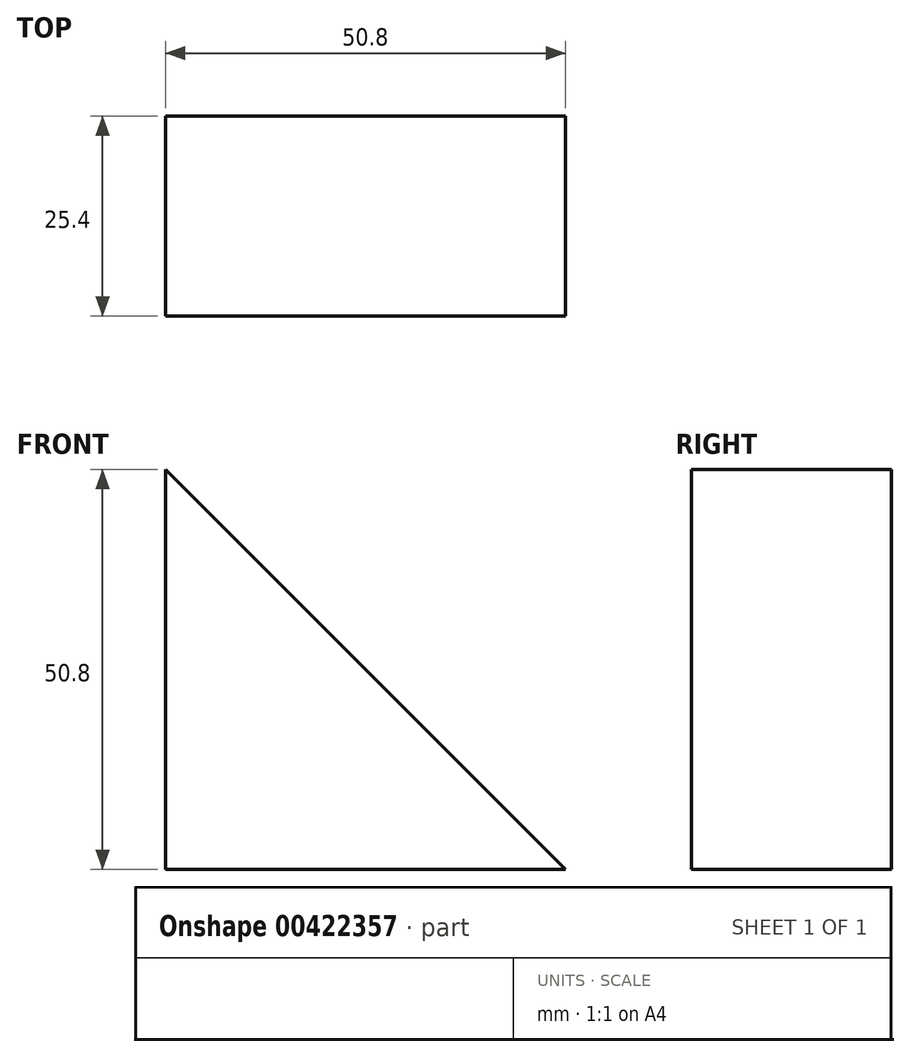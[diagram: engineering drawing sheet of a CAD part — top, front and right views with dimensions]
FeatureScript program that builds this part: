
annotation { "Feature Type Name" : "Feature", "Feature Type Description" : "" }
export const myFeature = defineFeature(function(context is Context, id is Id, definition is map)
    precondition{}
    {
        {
            var Q0;
            Q0=qCreatedBy(makeId("Front.planeOp"),FACE);
            var sketch = newSketch(context, id + "F0", { "sketchPlane" : qUnion([Q0])});
            skLineSegment(sketch, "E0", {"start": v(-50.8, 17.68) * mm, "end": v(-50.8, -33.12) * mm});
            skLineSegment(sketch, "E1", {"start": v(-50.8, -33.12) * mm, "end": v(0, -33.12) * mm});
            skLineSegment(sketch, "E2", {"start": v(-50.8, 17.68) * mm, "end": v(0, -33.12) * mm});
            skSolve(sketch);
        }
        {
            var Q0;
            Q0 = qSketchRegion(id + "F0", true);
            extrude(context, id + "F1", {"entities" : qUnion([Q0]), "depth" : 25.4 * mm});
        }
    });
